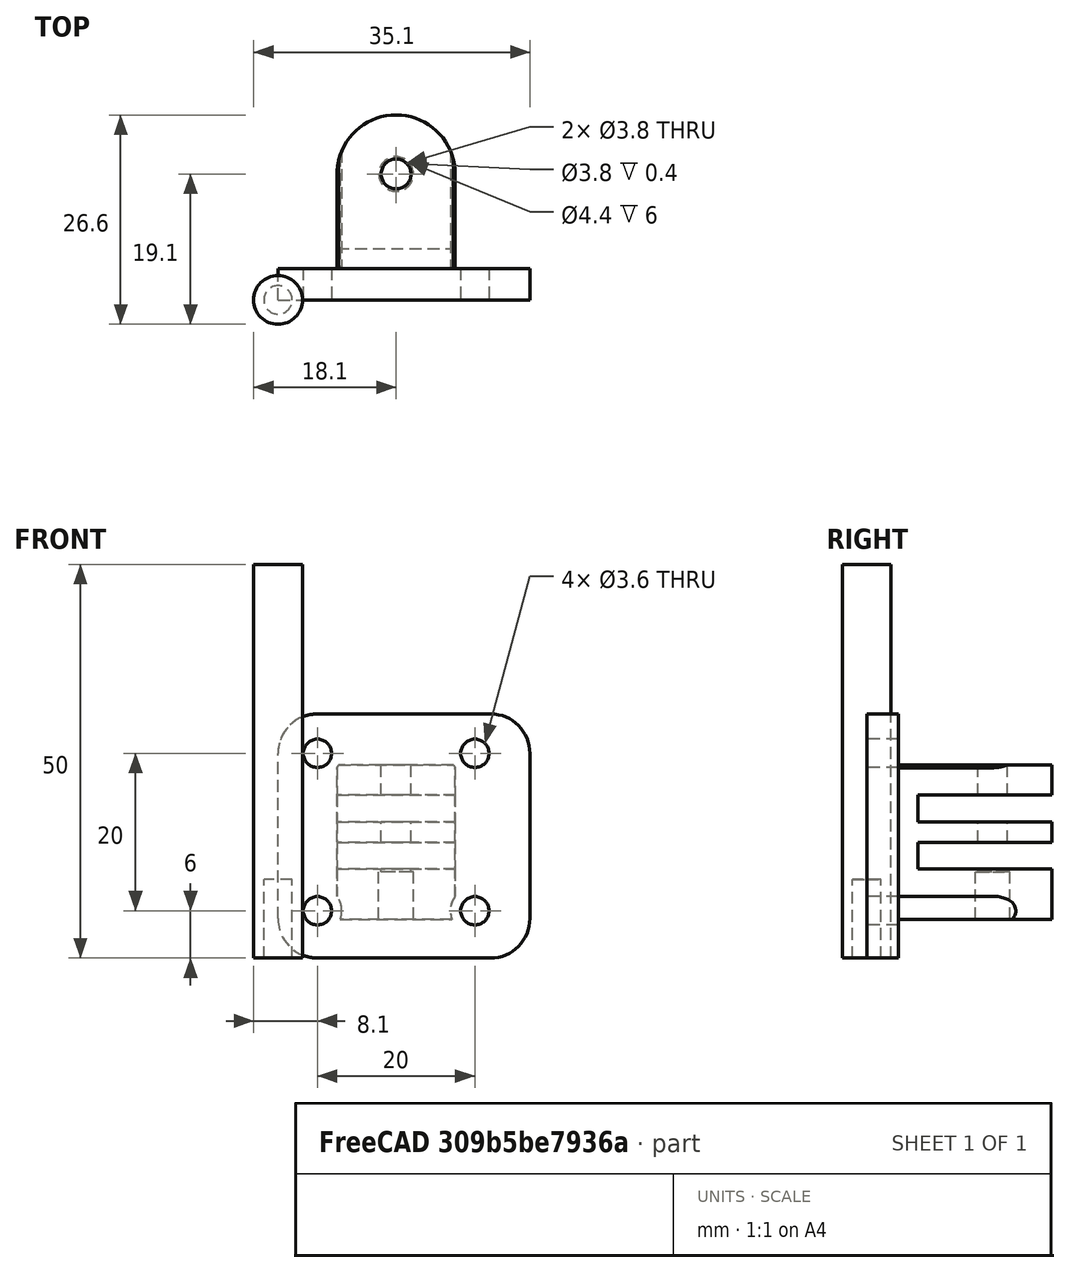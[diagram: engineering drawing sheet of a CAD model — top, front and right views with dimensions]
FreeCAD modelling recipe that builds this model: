
FCSTD DOCUMENT  (FreeCAD 0.19R23578 (Git))
Label: solar_panel_holder
License: All rights reserved
LicenseURL: http://en.wikipedia.org/wiki/All_rights_reserved
objects: Part::Cylinder×2, Part::FeaturePython×2, Part::MultiFuse×2, Part::Feature×1, Part::Box×1, Part::Fillet×1, Part::Cut×1
note: 8 computed .brp shape members not serialized (recipe doc carries the construction recipe); baked Part::Feature solids carry a one-line shape summary decoded from their .brp

FEATURE [Part::Feature] Cut003002  label="side 3"
  Placement = pos=(15,3.5,16) rot=(-1,0,0;1.5708rad)
  shape: bbox 15 x 20 x 19.6 mm, 23 faces (baked)
FEATURE [Part::Box] Box  label="bottom cube"
  AttacherType = Attacher::AttachEngine3D
  Height = 31
  Length = 32
  Width = 4
FEATURE [Part::Cylinder] Cylinder008  label="top bolt hole001"
  Angle = 360
  AttacherType = Attacher::AttachEngine3D
  Height = 10
  Radius = 1.8
FEATURE [Part::FeaturePython] Array005  label="bolt hole array"  # Draft array (typed FeaturePython)
  Angle = 360
  ArrayType = 0
  Axis = (0,0,1)
  Base = -> Cylinder008
  Center = (0,0,0)
  Count = 4
  ExpandArray = false
  Fuse = false
  IntervalAxis = (0,0,0)
  IntervalX = (20,0,0)
  IntervalY = (0,20,0)
  IntervalZ = (0,0,100)
  NumberCircles = 3
  NumberPolar = 5
  NumberX = 2
  NumberY = 2
  NumberZ = 1
  Placement = pos=(5,4,6) rot=(1,0,0;1.5708rad)
  PlacementList = 4 placements: [(0,0,0),(0,20,0),(20,0,0),(20,20,0)]
  RadialDistance = 50
  ScaleList = (4) [(1,1,1),(1,1,1),(1,1,1),(1,1,1)]
  Symmetry = 1
  TangentialDistance = 25
FEATURE [Part::Fillet] Fillet  label="bottom fillet"
  Base = -> Box
  Edges = 4 edges r=5: [Edge2,Edge4,Edge6,Edge8]
FEATURE [Part::MultiFuse] Fusion  label="body fusion"
  Shapes = -> [Cut003002,Fillet]
FEATURE [Part::Cylinder] Cylinder009  label="top bolt head hole"
  Angle = 360
  AttacherType = Attacher::AttachEngine3D
  Height = 50
  Radius = 3.1
FEATURE [Part::FeaturePython] Array006  label="bolt head hole array"  # Draft array (typed FeaturePython)
  Angle = 360
  ArrayType = 0
  Axis = (0,0,1)
  Base = -> Cylinder009
  Center = (0,0,0)
  Count = 4
  ExpandArray = false
  Fuse = false
  IntervalAxis = (0,0,0)
  IntervalX = (20,0,0)
  IntervalY = (0,20,0)
  IntervalZ = (0,0,100)
  NumberCircles = 3
  NumberPolar = 5
  NumberX = 2
  NumberY = 2
  NumberZ = 1
  Placement = pos=(5,54,6) rot=(1,0,0;1.5708rad)
  PlacementList = 4 placements: [(0,0,0),(0,20,0),(20,0,0),(20,20,0)]
  RadialDistance = 50
  ScaleList = (4) [(1,1,1),(1,1,1),(1,1,1),(1,1,1)]
  Symmetry = 1
  TangentialDistance = 25
FEATURE [Part::MultiFuse] Fusion001  label="hole fusion"
  Shapes = -> [Array005,Array006]
FEATURE [Part::Cut] Cut  label="solar panet attachment cut"
  Base = -> Fusion
  Tool = -> Fusion001
